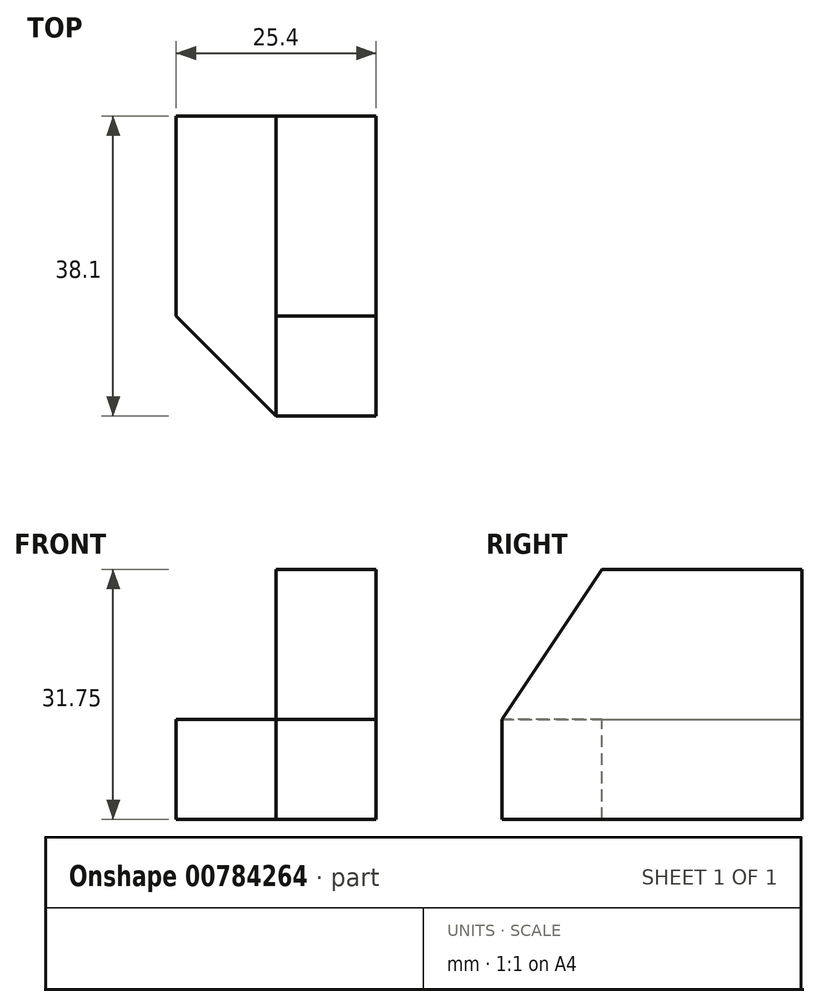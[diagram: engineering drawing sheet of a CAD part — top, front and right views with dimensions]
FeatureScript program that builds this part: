
annotation { "Feature Type Name" : "Feature", "Feature Type Description" : "" }
export const myFeature = defineFeature(function(context is Context, id is Id, definition is map)
    precondition{}
    {
        {
            var Q0;
            Q0=qCreatedBy(makeId("Front.planeOp"),FACE);
            var sketch = newSketch(context, id + "F0", { "sketchPlane" : qUnion([Q0])});
            skLineSegment(sketch, "E0", {"start": v(0, 0) * mm, "end": v(-12.7, 0) * mm});
            skLineSegment(sketch, "E1", {"start": v(0, 0) * mm, "end": v(0, 31.75) * mm});
            skLineSegment(sketch, "E2", {"start": v(0, 31.75) * mm, "end": v(-12.7, 31.75) * mm});
            skLineSegment(sketch, "E3", {"start": v(-12.7, 31.75) * mm, "end": v(-12.7, 0) * mm});
            skLineSegment(sketch, "E4", {"start": v(-12.7, 0) * mm, "end": v(-25.4, 0) * mm});
            skLineSegment(sketch, "E5", {"start": v(-25.4, 0) * mm, "end": v(-25.4, 12.7) * mm});
            skLineSegment(sketch, "E6", {"start": v(-25.4, 12.7) * mm, "end": v(-12.7, 12.7) * mm});
            skLineSegment(sketch, "E7", {"start": v(-12.7, 12.7) * mm, "end": v(-12.7, 0) * mm});
            skSolve(sketch);
        }
        {
            var Q0;
            Q0=makeQuery(id+"F0.imprint","IMPRINT",FACE,{"disambiguationData":[TD([[makeQuery(id+"F0.imprint","IMPRINT",EDGE,{"derivedFrom":sQuery(id+"F0.wireOp",EDGE,"E4")}),-1.0]])]});
            var Q1;
            Q1=makeQuery(id+"F0.imprint","IMPRINT",FACE,{"disambiguationData":[TD([[makeQuery(id+"F0.imprint","IMPRINT",EDGE,{"derivedFrom":sQuery(id+"F0.wireOp",EDGE,"E0")}),-1.0]])]});
            extrude(context, id + "F1", {"entities" : qUnion([Q0, Q1]), "depth" : 38.1 * mm, "offsetDistance" : 25.4 * mm});
        }
        {
            var Q0;
            Q0=makeQuery(id+"F1.opExtrude","SWEPT_FACE",FACE,{"disambiguationData":[OSD([sQuery(id+"F0.wireOp",EDGE,"E6")])]});
            var sketch = newSketch(context, id + "F2", { "sketchPlane" : qUnion([Q0])});
            skLineSegment(sketch, "E8", {"start": v(-12.7, -38.1) * mm, "end": v(-25.4, -38.1) * mm});
            skLineSegment(sketch, "E9", {"start": v(-25.4, -38.1) * mm, "end": v(-25.4, -25.4) * mm});
            skLineSegment(sketch, "E10", {"start": v(-25.4, -25.4) * mm, "end": v(-12.7, -38.1) * mm});
            skSolve(sketch);
        }
        {
            var Q0;
            Q0=makeQuery(id+"F1.opExtrude","SWEPT_FACE",FACE,{"disambiguationData":[OSD([sQuery(id+"F0.wireOp",EDGE,"E3")])]});
            var sketch = newSketch(context, id + "F3", { "sketchPlane" : qUnion([Q0])});
            skLineSegment(sketch, "E11", {"start": v(38.1, 31.75) * mm, "end": v(25.4, 31.75) * mm});
            skLineSegment(sketch, "E12", {"start": v(25.4, 31.75) * mm, "end": v(38.1, 12.7) * mm});
            skLineSegment(sketch, "E13", {"start": v(38.1, 12.7) * mm, "end": v(38.1, 31.75) * mm});
            skSolve(sketch);
        }
        {
            var Q0;
            Q0=makeQuery(id+"F3.imprint","IMPRINT",FACE,{"disambiguationData":[TD([[makeQuery(id+"F3.imprint","IMPRINT",EDGE,{"derivedFrom":sQuery(id+"F3.wireOp",EDGE,"E11")}),1.0]])]});
            extrude(context, id + "F4", {"entities" : qUnion([Q0]), "operationType" : NewBodyOperationType.REMOVE, "oppositeDirection" : true, "depth" : 25.4 * mm, "offsetDistance" : 25.4 * mm});
        }
        {
            var Q0;
            Q0=makeQuery(id+"F2.imprint","IMPRINT",FACE,{"disambiguationData":[TD([[makeQuery(id+"F2.imprint","IMPRINT",EDGE,{"derivedFrom":sQuery(id+"F2.wireOp",EDGE,"E8")}),1.0]])]});
            extrude(context, id + "F5", {"entities" : qUnion([Q0]), "operationType" : NewBodyOperationType.REMOVE, "oppositeDirection" : true, "depth" : 25.4 * mm, "offsetDistance" : 25.4 * mm});
        }
    });
